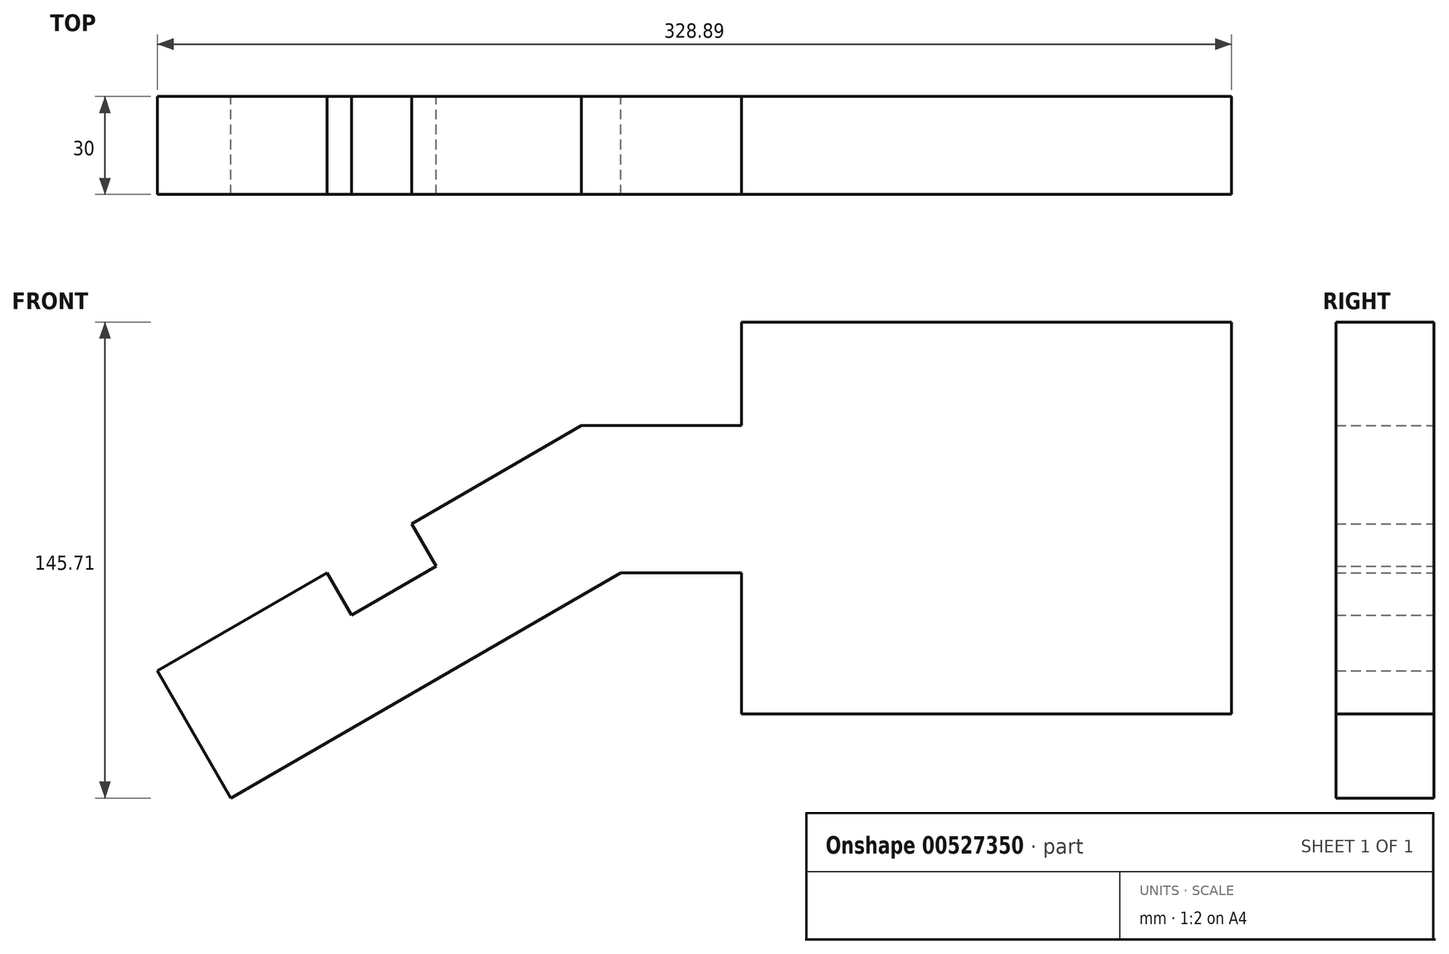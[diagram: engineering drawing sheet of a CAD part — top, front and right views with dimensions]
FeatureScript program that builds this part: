
annotation { "Feature Type Name" : "Feature", "Feature Type Description" : "" }
export const myFeature = defineFeature(function(context is Context, id is Id, definition is map)
    precondition{}
    {
        {
            var Q0;
            Q0=qCreatedBy(makeId("Front.planeOp"),FACE);
            var sketch = newSketch(context, id + "F0", { "sketchPlane" : qUnion([Q0])});
            skLineSegment(sketch, "E0", {"start": v(-106.48, -14.86) * mm, "end": v(-83.98, -53.83) * mm});
            skLineSegment(sketch, "E1", {"start": v(-106.48, -14.86) * mm, "end": v(-54.51, 15.14) * mm});
            skLineSegment(sketch, "E2", {"start": v(-54.51, 15.14) * mm, "end": v(-47.01, 2.15) * mm});
            skLineSegment(sketch, "E3", {"start": v(-47.01, 2.15) * mm, "end": v(-21.03, 17.15) * mm});
            skLineSegment(sketch, "E4", {"start": v(-21.03, 17.15) * mm, "end": v(-28.53, 30.14) * mm});
            skLineSegment(sketch, "E5", {"start": v(-83.98, -53.83) * mm, "end": v(35.49, 15.14) * mm});
            skLineSegment(sketch, "E6", {"start": v(-28.53, 30.14) * mm, "end": v(23.43, 60.14) * mm});
            skLineSegment(sketch, "E7", {"start": v(23.43, 60.14) * mm, "end": v(143.43, 60.14) * mm});
            skLineSegment(sketch, "E8", {"start": v(143.43, 60.14) * mm, "end": v(143.43, 15.14) * mm});
            skLineSegment(sketch, "E9", {"start": v(143.43, 15.14) * mm, "end": v(35.49, 15.14) * mm});
            skLineSegment(sketch, "E10", {"start": v(72.4, 15.14) * mm, "end": v(72.4, -28.12) * mm});
            skLineSegment(sketch, "E11", {"start": v(72.4, -28.12) * mm, "end": v(222.4, -28.12) * mm});
            skLineSegment(sketch, "E12", {"start": v(222.4, -28.12) * mm, "end": v(222.4, 91.88) * mm});
            skLineSegment(sketch, "E13", {"start": v(72.4, 60.14) * mm, "end": v(72.4, 84.43) * mm});
            skLineSegment(sketch, "E14", {"start": v(222.4, 91.88) * mm, "end": v(72.4, 91.88) * mm});
            skLineSegment(sketch, "E15", {"start": v(72.4, 91.88) * mm, "end": v(72.4, 84.43) * mm});
            skSolve(sketch);
        }
        {
            var Q0;
            Q0 = qSketchRegion(id + "F0", true);
            extrude(context, id + "F1", {"entities" : qUnion([Q0]), "depth" : 30 * mm, "offsetDistance" : 25 * mm});
        }
    });
